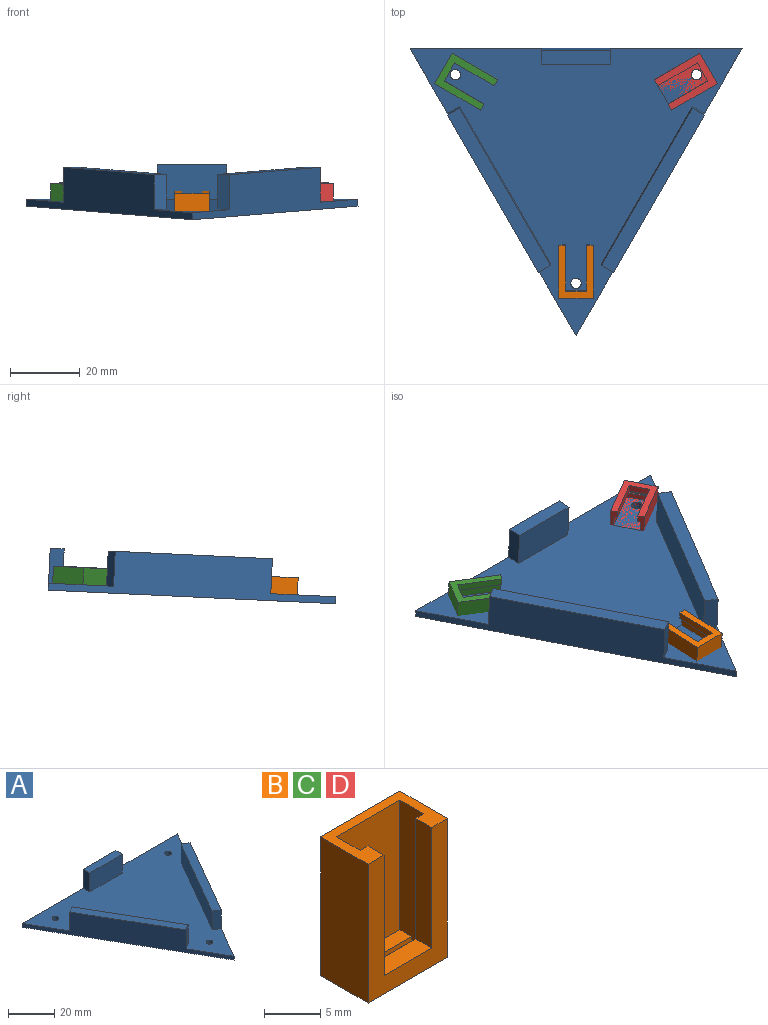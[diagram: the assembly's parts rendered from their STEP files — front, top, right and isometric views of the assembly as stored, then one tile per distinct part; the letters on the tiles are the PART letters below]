
ASSEMBLY  parts=4 mates=4
PART A: 20 faces, bbox 95x82.3x12 mm
  f0: plane 94.98x82.26mm, normal (0,0,1), area 3389.2mm2, adj f1,f2,f3,f4,f5,f6,f8,f9
  f1: plane 94.98x12mm, normal (0,1,0), area 390mm2, adj f0,f2,f5,f7,f16,f17,f19
  f2: plane 82.26x47.49mm, normal (-0.87,-0.5,0), area 710mm2, adj f0,f1,f5,f7,f8,f9,f11
  f3: cylinder r=1.5mm len=3mm, axis (0,0,-1), area 18.8mm2, adj f0,f7
  f4: cylinder r=1.5mm len=3mm, axis (0,0,-1), area 18.8mm2, adj f0,f7
  f5: plane 82.26x47.49mm, normal (0.87,-0.5,0), area 710mm2, adj f0,f1,f2,f7,f12,f13,f15
  f6: cylinder r=1.5mm len=3mm, axis (0,0,-1), area 18.8mm2, adj f0,f7
  f7: plane 94.98x82.26mm, normal (0,0,-1), area 3885.2mm2, adj f1,f2,f3,f4,f5,f6
  f8: plane 10x3.46mm, normal (-0.5,0.87,0), area 40mm2, adj f0,f2,f10,f11
  f9: plane 10x3.46mm, normal (0.5,-0.87,0), area 40mm2, adj f0,f2,f10,f11
  f10: plane 45.03x26mm, normal (0.87,0.5,0), area 520mm2, adj f0,f8,f9,f11
  f11: plane 47.03x29.46mm, normal (0,0,1), area 208mm2, adj f2,f8,f9,f10
  f12: plane 10x3.46mm, normal (-0.5,-0.87,0), area 40mm2, adj f0,f5,f14,f15
  f13: plane 10x3.46mm, normal (0.5,0.87,0), area 40mm2, adj f0,f5,f14,f15
  f14: plane 45.03x26mm, normal (-0.87,0.5,0), area 520mm2, adj f0,f12,f13,f15
  f15: plane 47.03x29.46mm, normal (0,0,1), area 208mm2, adj f5,f12,f13,f14
  f16: plane 10x4mm, normal (1,0,0), area 40mm2, adj f0,f1,f18,f19
  f17: plane 10x4mm, normal (-1,0,0), area 40mm2, adj f0,f1,f18,f19
  f18: plane 20x10mm, normal (0,-1,0), area 200mm2, adj f0,f16,f17,f19
  f19: plane 20x4mm, normal (0,0,1), area 80mm2, adj f1,f16,f17,f18
PART B: 17 faces, bbox 10x6x15.1 mm
  f0: plane 8x1.5mm, normal (0,0,1), area 12mm2, adj f6,f7,f13,f16
  f1: plane 15.13x10mm, normal (0,1,0), area 144.3mm2, adj f2,f3,f4,f5,f14
  f2: cylinder r=1.5mm len=3mm, axis (0,-1,0), area 9.4mm2, adj f1,f13
  f3: plane 10x6mm, normal (0,0,-1), area 60mm2, adj f1,f4,f5,f11
  f4: plane 15.13x6mm, normal (1,0,0), area 90.8mm2, adj f1,f3,f11,f14
  f5: plane 15.13x6mm, normal (-1,0,0), area 90.8mm2, adj f1,f3,f11,f14
  f6: plane 14.63x3mm, normal (-1,0,0), area 43.1mm2, adj f0,f12,f13,f14,f15,f16
  f7: plane 14.63x3mm, normal (1,0,0), area 43.1mm2, adj f0,f12,f13,f14,f15,f16
  f8: plane 13.13x2mm, normal (-1,0,0), area 26.3mm2, adj f9,f11,f12,f14
  f9: plane 6x2mm, normal (0,0,1), area 12mm2, adj f8,f10,f11,f12
  f10: plane 13.13x2mm, normal (1,0,0), area 26.3mm2, adj f9,f11,f12,f14
  f11: plane 15.13x10mm, normal (0,-1,0), area 72.5mm2, adj f3,f4,f5,f8,f9,f10,f14
  f12: plane 14.63x8mm, normal (0,1,0), area 38.3mm2, adj f6,f7,f8,f9,f10,f14,f15
  f13: plane 14.13x8mm, normal (0,-1,0), area 106mm2, adj f0,f2,f6,f7,f14
  f14: plane 10x6mm, normal (0,0,1), area 24mm2, adj f1,f4,f5,f6,f7,f8,f10,f11
  f15: plane 8x1.5mm, normal (0,0,1), area 12mm2, adj f6,f7,f12,f16
  f16: plane 8x0.5mm, normal (0,-1,0), area 4mm2, adj f0,f6,f7,f15
PART C: same geometry as B
PART D: same geometry as B
PLACE A rot(axis=(1,0,0),2.7deg) t=(-7.17,20.74,2.09)mm fixed
PLACE B rot(axis=(-1,0,0),87.3deg) t=(-7.17,-4.65,1.79)mm
PLACE C rot(axis=(-0.37,0.67,-0.64),137.6deg) t=(-37.78,48.29,4.29)mm
PLACE D rot(axis=(-0.37,-0.67,0.64),137.6deg) t=(23.43,48.29,4.39)mm
MATE planar D.f13 <-> A.f0  axis (0,-0.05,1) through (23.57,48.32,5.39)mm
MATE cylindrical A.f3 <-> B.f2  axis (0,0.05,-1) through (-7.17,-9.15,1.68)mm
MATE cylindrical A.f6 <-> C.f2  axis (0,-0.05,1) through (-41.67,50.49,5.49)mm
MATE cylindrical A.f4 <-> D.f2  axis (0,0.05,-1) through (27.33,50.54,4.5)mm
